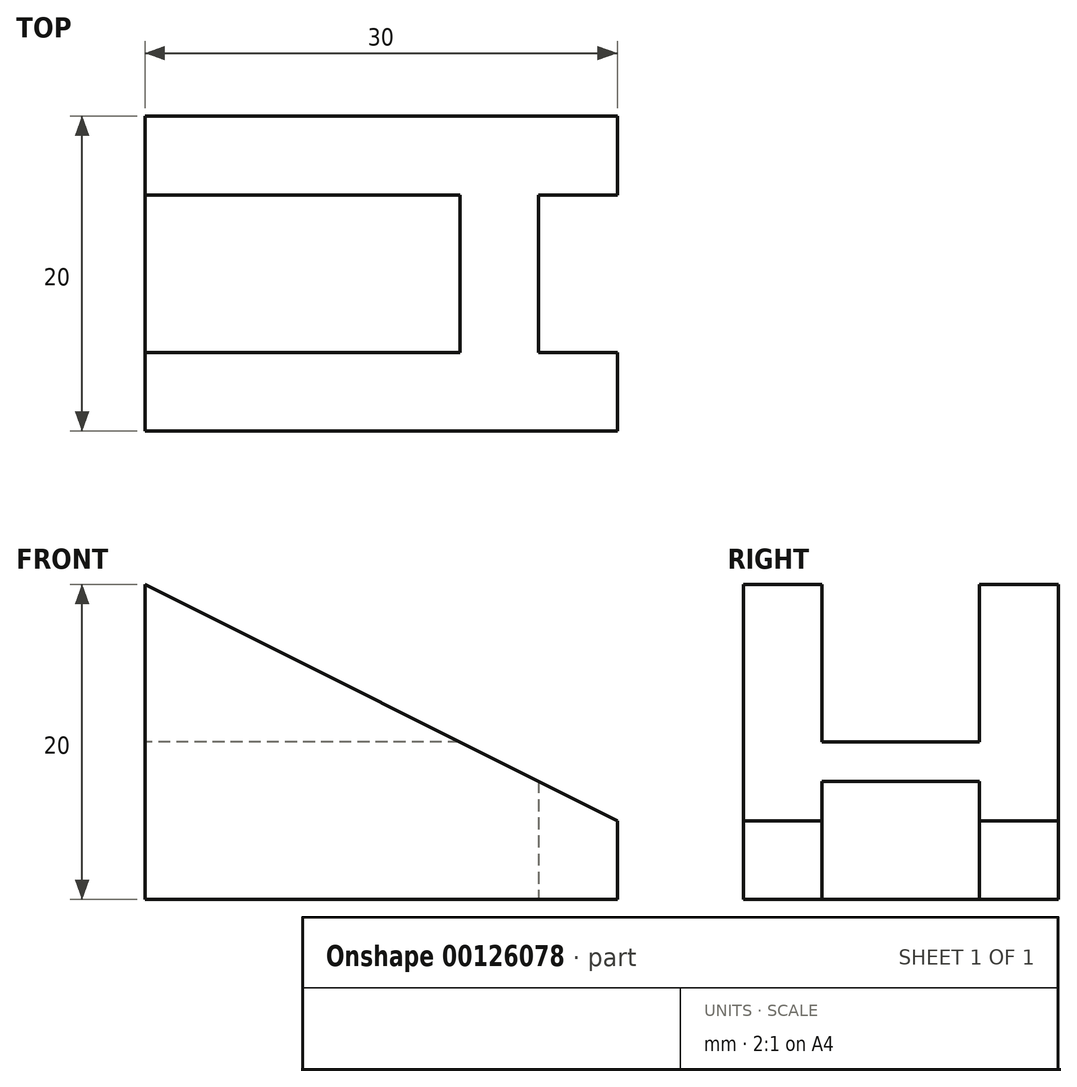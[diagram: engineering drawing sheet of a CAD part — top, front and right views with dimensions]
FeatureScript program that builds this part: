
annotation { "Feature Type Name" : "Feature", "Feature Type Description" : "" }
export const myFeature = defineFeature(function(context is Context, id is Id, definition is map)
    precondition{}
    {
        {
            var Q0;
            Q0=qCreatedBy(makeId("Right.planeOp"),FACE);
            var sketch = newSketch(context, id + "F0", { "sketchPlane" : qUnion([Q0])});
            skLineSegment(sketch, "E0", {"start": v(0, 0) * mm, "end": v(-10, 0) * mm});
            skLineSegment(sketch, "E1", {"start": v(-10, 0) * mm, "end": v(-10, 20) * mm});
            skLineSegment(sketch, "E2", {"start": v(-10, 20) * mm, "end": v(-5, 20) * mm});
            skLineSegment(sketch, "E3", {"start": v(-5, 20) * mm, "end": v(-5, 10) * mm});
            skLineSegment(sketch, "E4", {"start": v(-5, 10) * mm, "end": v(0, 10) * mm});
            skLineSegment(sketch, "E5.MirrorCS", {"start": v(10, 20) * mm, "end": v(5, 20) * mm});
            skLineSegment(sketch, "E6.MirrorCS", {"start": v(10, 0) * mm, "end": v(10, 20) * mm});
            skLineSegment(sketch, "E7.MirrorCS", {"start": v(5, 20) * mm, "end": v(5, 10) * mm});
            skLineSegment(sketch, "E8.MirrorCS", {"start": v(5, 10) * mm, "end": v(0, 10) * mm});
            skLineSegment(sketch, "E9.MirrorCS", {"start": v(0, 0) * mm, "end": v(10, 0) * mm});
            skSolve(sketch);
        }
        {
            var Q0;
            Q0 = qSketchRegion(id + "F0", true);
            extrude(context, id + "F1", {"entities" : qUnion([Q0]), "endBound" : BoundingType.SYMMETRIC, "depth" : 30 * mm});
        }
        {
            var Q0;
            Q0=makeQuery(id+"F1.opExtrude","SWEPT_FACE",FACE,{"disambiguationData":[OSD([sQuery(id+"F0.wireOp",EDGE,"E1")])]});
            var sketch = newSketch(context, id + "F2", { "sketchPlane" : qUnion([Q0])});
            skLineSegment(sketch, "E10", {"start": v(-15, 20) * mm, "end": v(-15, 0) * mm});
            skLineSegment(sketch, "E11", {"start": v(-15, 0) * mm, "end": v(15, 0) * mm});
            skLineSegment(sketch, "E12", {"start": v(15, 0) * mm, "end": v(15, 5) * mm});
            skLineSegment(sketch, "E13", {"start": v(15, 5) * mm, "end": v(-15, 20) * mm});
            skSolve(sketch);
        }
        {
            var Q0;
            {var subQ0=sQuery(id+"F2.wireOp",EDGE,"E13");Q0=makeQuery(id+"F2.imprint","IMPRINT",FACE,{"disambiguationData":[TD([[makeQuery(id+"F2.imprint","IMPRINT",EDGE,{"derivedFrom":subQ0}),-1.0]])]});}
            extrude(context, id + "F3", {"entities" : qUnion([Q0]), "operationType" : NewBodyOperationType.REMOVE, "endBound" : BoundingType.THROUGH_ALL, "oppositeDirection" : true, "depth" : 25 * mm});
        }
        {
            var Q0;
            Q0=makeQuery(id+"F1.opExtrude","CAP_FACE",FACE,{"disambiguationData":[OSD([sQuery(id+"F0.wireOp",EDGE,"E0"),sQuery(id+"F0.wireOp",EDGE,"E1"),sQuery(id+"F0.wireOp",EDGE,"E2"),sQuery(id+"F0.wireOp",EDGE,"E3"),sQuery(id+"F0.wireOp",EDGE,"E4"),sQuery(id+"F0.wireOp",EDGE,"E5.MirrorCS"),sQuery(id+"F0.wireOp",EDGE,"E6.MirrorCS"),sQuery(id+"F0.wireOp",EDGE,"E7.MirrorCS"),sQuery(id+"F0.wireOp",EDGE,"E8.MirrorCS"),sQuery(id+"F0.wireOp",EDGE,"E9.MirrorCS")])],"isStart":false});
            var sketch = newSketch(context, id + "F4", { "sketchPlane" : qUnion([Q0])});
            skLineSegment(sketch, "E14.bottom", {"start": v(-5, 5) * mm, "end": v(5, 5) * mm});
            skLineSegment(sketch, "E14.top", {"start": v(-5, 0) * mm, "end": v(5, 0) * mm});
            skLineSegment(sketch, "E14.left", {"start": v(-5, 5) * mm, "end": v(-5, 0) * mm});
            skLineSegment(sketch, "E14.right", {"start": v(5, 5) * mm, "end": v(5, 0) * mm});
            skPoint(sketch, "E15", {"position": v(0, 5) * mm});
            skSolve(sketch);
        }
        {
            var Q0;
            Q0=makeQuery(id+"F4.imprint","IMPRINT",FACE,{"disambiguationData":[TD([[makeQuery(id+"F4.imprint","IMPRINT",EDGE,{"derivedFrom":sQuery(id+"F4.wireOp",EDGE,"E14.bottom")}),1.0]])]});
            extrude(context, id + "F5", {"entities" : qUnion([Q0]), "operationType" : NewBodyOperationType.REMOVE, "oppositeDirection" : true, "depth" : 5 * mm});
        }
        {
            var Q0;
            Q0=qCreatedBy(makeId("Top.planeOp"),FACE);
            var sketch = newSketch(context, id + "F6", { "sketchPlane" : qUnion([Q0])});
            skLineSegment(sketch, "E16", {"start": v(15, 0) * mm, "end": v(15, 5) * mm});
            skLineSegment(sketch, "E17", {"start": v(15, 5) * mm, "end": v(10, 5) * mm});
            skLineSegment(sketch, "E18", {"start": v(10, 5) * mm, "end": v(10, 0) * mm});
            skLineSegment(sketch, "E19.MirrorCS", {"start": v(15, -5) * mm, "end": v(10, -5) * mm});
            skLineSegment(sketch, "E20.MirrorCS", {"start": v(10, -5) * mm, "end": v(10, 0) * mm});
            skLineSegment(sketch, "E21.MirrorCS", {"start": v(15, 0) * mm, "end": v(15, -5) * mm});
            skSolve(sketch);
        }
        {
            var Q0;
            Q0=makeQuery(id+"F6.imprint","IMPRINT",FACE,{"disambiguationData":[TD([[makeQuery(id+"F6.imprint","IMPRINT",EDGE,{"derivedFrom":sQuery(id+"F6.wireOp",EDGE,"E16")}),1.0]])]});
            var Q1;
            Q1=sQuery(id+"F6.wireOp",EDGE,"E17");
            var Q2;
            Q2=sQuery(id+"F6.wireOp",EDGE,"E18");
            var Q3;
            Q3=sQuery(id+"F6.wireOp",EDGE,"E20.MirrorCS");
            var Q4;
            Q4=sQuery(id+"F6.wireOp",EDGE,"E19.MirrorCS");
            extrude(context, id + "F7", {"entities" : qUnion([Q0]), "operationType" : NewBodyOperationType.REMOVE, "surfaceEntities" : qUnion([Q1, Q2, Q3, Q4]), "endBound" : BoundingType.THROUGH_ALL, "depth" : 11.5 * mm});
        }
    });
